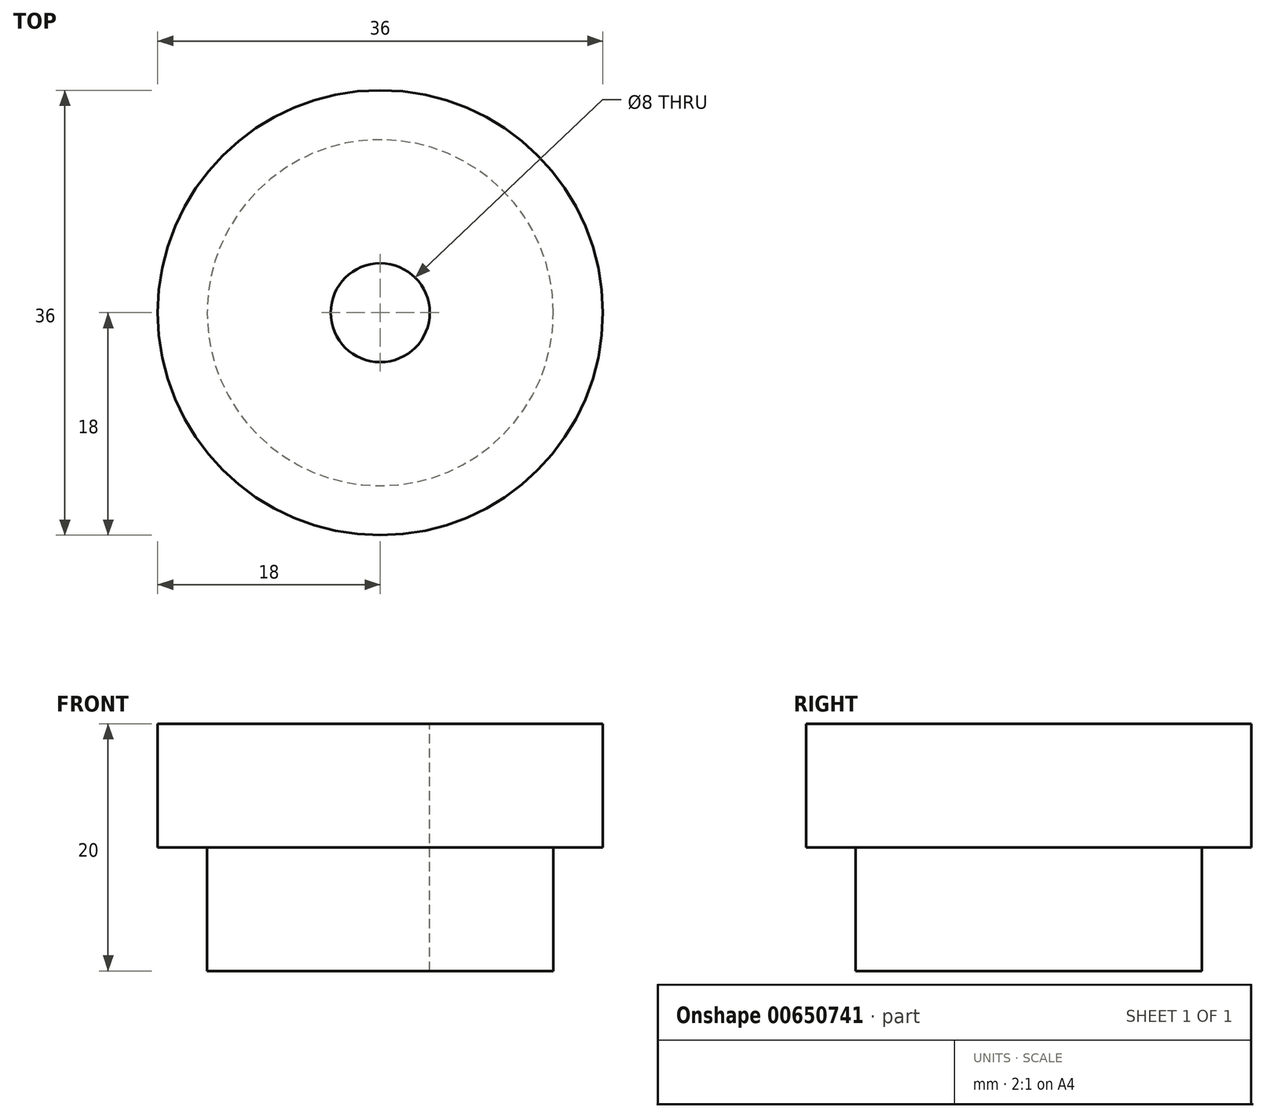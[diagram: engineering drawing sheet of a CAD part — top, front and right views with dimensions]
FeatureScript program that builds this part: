
annotation { "Feature Type Name" : "Feature", "Feature Type Description" : "" }
export const myFeature = defineFeature(function(context is Context, id is Id, definition is map)
    precondition{}
    {
        {
            var Q0;
            Q0=qCreatedBy(makeId("Front.planeOp"),FACE);
            var sketch = newSketch(context, id + "F0", { "sketchPlane" : qUnion([Q0])});
            skLineSegment(sketch, "E0", {"start": v(0, 51.74) * mm, "end": v(0, -70.43) * mm, "construction": true});
            skLineSegment(sketch, "E1", {"start": v(0, 0) * mm, "end": v(-18, 0) * mm});
            skLineSegment(sketch, "E2", {"start": v(-18, 0) * mm, "end": v(-18, -10) * mm});
            skLineSegment(sketch, "E3", {"start": v(-18, -10) * mm, "end": v(-14, -10) * mm});
            skLineSegment(sketch, "E4", {"start": v(-14, -10) * mm, "end": v(-14, -20) * mm});
            skLineSegment(sketch, "E5", {"start": v(-14, -20) * mm, "end": v(0, -20) * mm});
            skLineSegment(sketch, "E6", {"start": v(0, -20) * mm, "end": v(0, 0) * mm});
            skLineSegment(sketch, "E7", {"start": v(-4, 0) * mm, "end": v(-4, -20) * mm});
            skSolve(sketch);
        }
        {
            var Q0;
            {var subQ1=sQuery(id+"F0.wireOp",EDGE,"E2");Q0=makeQuery(id+"F0.imprint","IMPRINT",FACE,{"disambiguationData":[TD([[makeQuery(id+"F0.imprint","IMPRINT",EDGE,{"derivedFrom":subQ1}),1.0]])]});}
            var Q1;
            Q1=sQuery(id+"F0.wireOp",EDGE,"E0");
            revolve(context, id + "F1", {"entities" : qUnion([Q0]), "axis" : qUnion([Q1]), "revolveType" : RevolveType.FULL});
        }
    });
